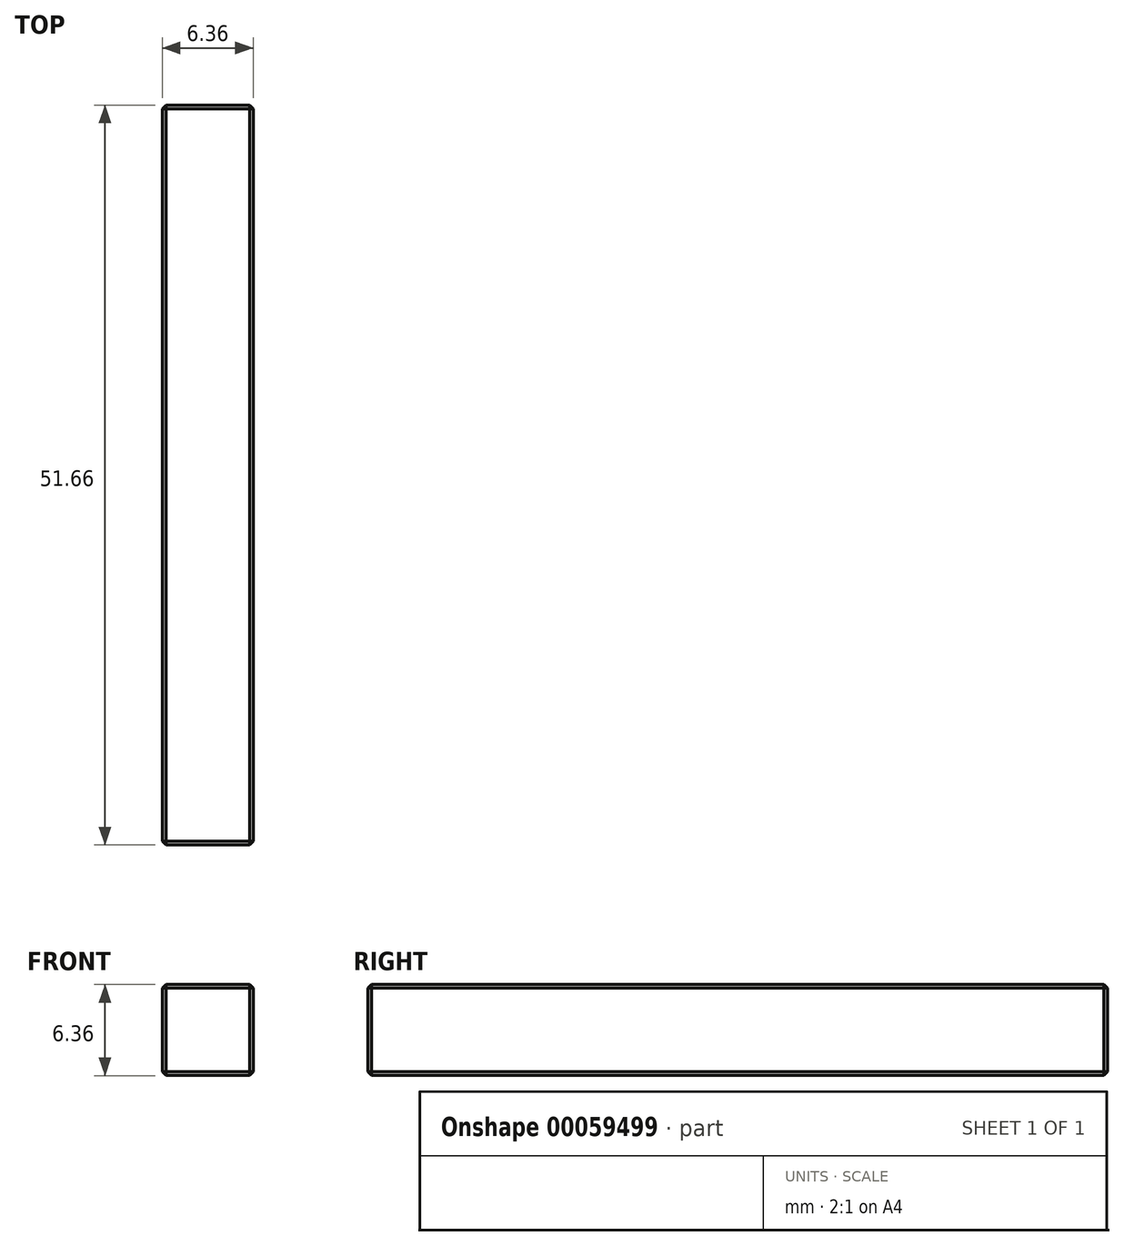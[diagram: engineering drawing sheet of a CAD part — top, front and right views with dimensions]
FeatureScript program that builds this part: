
annotation { "Feature Type Name" : "Feature", "Feature Type Description" : "" }
export const myFeature = defineFeature(function(context is Context, id is Id, definition is map)
    precondition{}
    {
        {
            var Q0;
            Q0=qCreatedBy(makeId("Front.planeOp"),FACE);
            var sketch = newSketch(context, id + "F0", { "sketchPlane" : qUnion([Q0])});
            skLineSegment(sketch, "E0.rect.bottom", {"start": v(3.17, 3.18) * mm, "end": v(-3.18, 3.18) * mm});
            skLineSegment(sketch, "E0.rect.top", {"start": v(3.18, -3.18) * mm, "end": v(-3.17, -3.18) * mm});
            skLineSegment(sketch, "E0.rect.left", {"start": v(3.17, 3.18) * mm, "end": v(3.18, -3.18) * mm});
            skLineSegment(sketch, "E0.rect.right", {"start": v(-3.18, 3.18) * mm, "end": v(-3.17, -3.18) * mm});
            skPoint(sketch, "E0.rect.middle", {"position": v(0, 0) * mm});
            skSolve(sketch);
        }
        {
            var Q0;
            Q0 = qSketchRegion(id + "F0", true);
            extrude(context, id + "F1", {"entities" : qUnion([Q0]), "oppositeDirection" : true, "depth" : 51.66 * mm});
        }
        {
            var Q0;
            Q0=makeQuery(id+"F1.opExtrude","CAP_EDGE",EDGE,{"disambiguationData":[OSD([sQuery(id+"F0.wireOp",EDGE,"E0.rect.bottom")])],"isStart":true});
            var Q1;
            Q1=makeQuery(id+"F1.opExtrude","CAP_EDGE",EDGE,{"disambiguationData":[OSD([sQuery(id+"F0.wireOp",EDGE,"E0.rect.right")])],"isStart":true});
            var Q2;
            Q2=makeQuery(id+"F1.opExtrude","CAP_EDGE",EDGE,{"disambiguationData":[OSD([sQuery(id+"F0.wireOp",EDGE,"E0.rect.top")])],"isStart":true});
            var Q3;
            Q3=makeQuery(id+"F1.opExtrude","CAP_EDGE",EDGE,{"disambiguationData":[OSD([sQuery(id+"F0.wireOp",EDGE,"E0.rect.left")])],"isStart":true});
            var Q4;
            Q4=makeQuery(id+"F1.opExtrude","CAP_EDGE",EDGE,{"disambiguationData":[OSD([sQuery(id+"F0.wireOp",EDGE,"E0.rect.top")])],"isStart":false});
            var Q5;
            Q5=makeQuery(id+"F1.opExtrude","CAP_EDGE",EDGE,{"disambiguationData":[OSD([sQuery(id+"F0.wireOp",EDGE,"E0.rect.left")])],"isStart":false});
            var Q6;
            Q6=makeQuery(id+"F1.opExtrude","CAP_EDGE",EDGE,{"disambiguationData":[OSD([sQuery(id+"F0.wireOp",EDGE,"E0.rect.bottom")])],"isStart":false});
            var Q7;
            Q7=makeQuery(id+"F1.opExtrude","CAP_EDGE",EDGE,{"disambiguationData":[OSD([sQuery(id+"F0.wireOp",EDGE,"E0.rect.right")])],"isStart":false});
            var Q8;
            Q8=makeQuery(id+"F1.opExtrude","SWEPT_EDGE",EDGE,{"disambiguationData":[OSD([sQuery(id+"F0.wireOp",EDGE,"E0.rect.top"),sQuery(id+"F0.wireOp",EDGE,"E0.rect.left")])]});
            var Q9;
            Q9=makeQuery(id+"F1.opExtrude","SWEPT_EDGE",EDGE,{"disambiguationData":[OSD([sQuery(id+"F0.wireOp",EDGE,"E0.rect.bottom"),sQuery(id+"F0.wireOp",EDGE,"E0.rect.left")])]});
            var Q10;
            Q10=makeQuery(id+"F1.opExtrude","SWEPT_EDGE",EDGE,{"disambiguationData":[OSD([sQuery(id+"F0.wireOp",EDGE,"E0.rect.bottom"),sQuery(id+"F0.wireOp",EDGE,"E0.rect.right")])]});
            var Q11;
            Q11=makeQuery(id+"F1.opExtrude","SWEPT_EDGE",EDGE,{"disambiguationData":[OSD([sQuery(id+"F0.wireOp",EDGE,"E0.rect.top"),sQuery(id+"F0.wireOp",EDGE,"E0.rect.right")])]});
            chamfer(context, id + "F2", {"entities" : qUnion([Q0, Q1, Q2, Q3, Q4, Q5, Q6, Q7, Q8, Q9, Q10, Q11]), "width" : 0.25 * mm, "tangentPropagation" : true});
        }
    });
